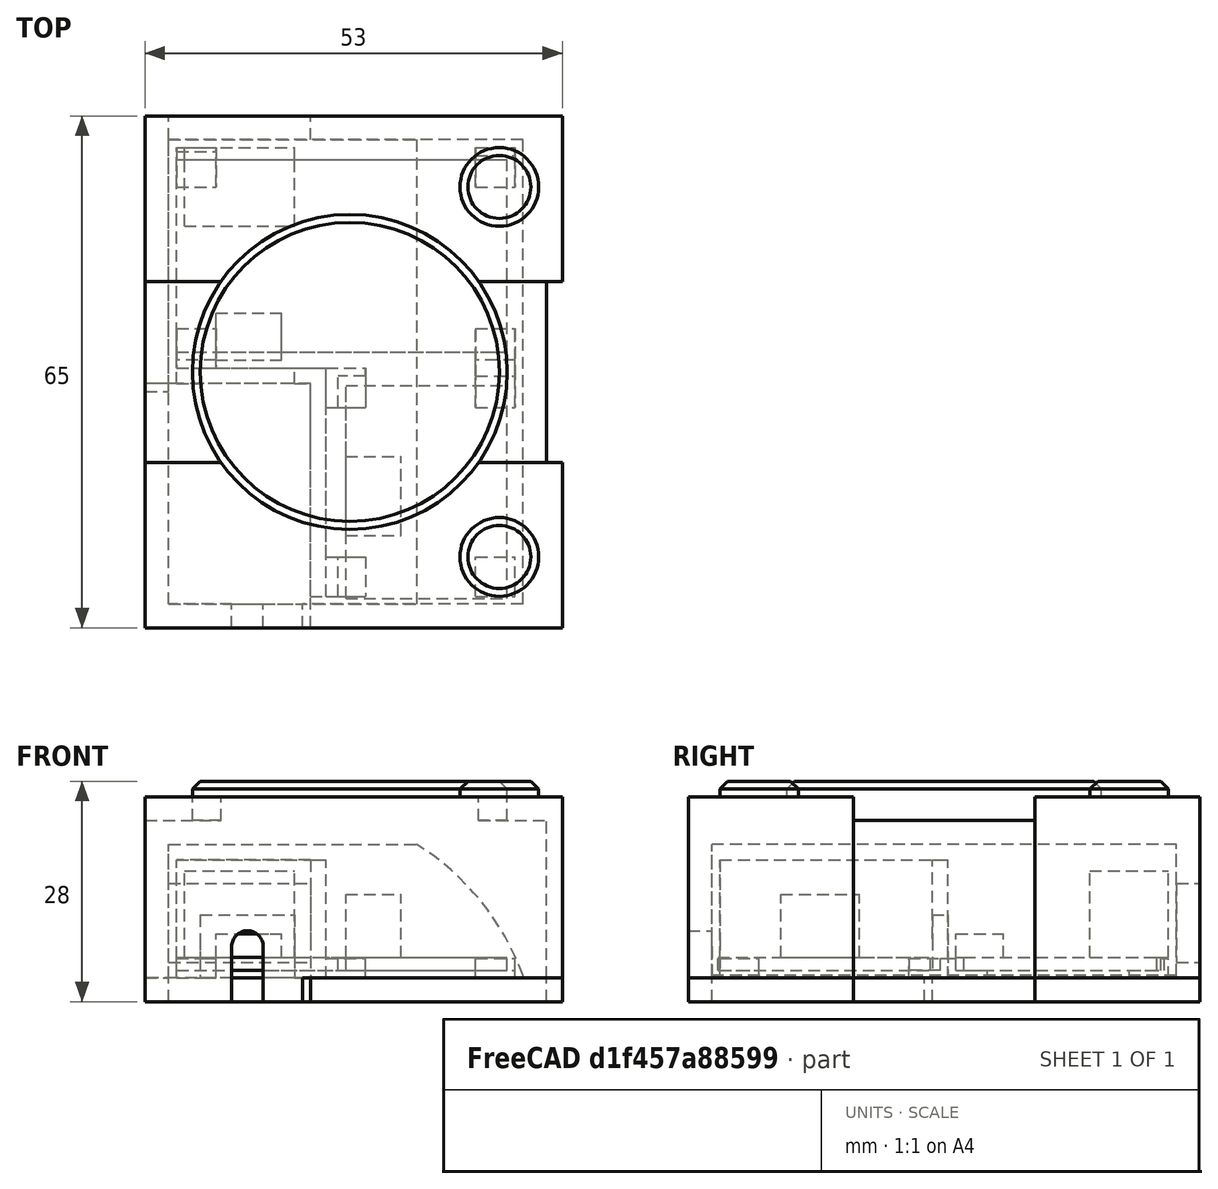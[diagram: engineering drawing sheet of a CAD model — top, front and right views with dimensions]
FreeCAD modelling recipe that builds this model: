
FCSTD DOCUMENT  (FreeCAD 0.17R13522 (Git))
Label: ps1
License: All rights reserved
LicenseURL: http://en.wikipedia.org/wiki/All_rights_reserved
objects: Part::Box×35, Part::Cut×16, Part::MultiFuse×8, PartDesign::FeatureBase×4, Part::Cylinder×4, Part::Fillet×2, App::DocumentObjectGroup×1, Part::MultiCommon×1, Part::Chamfer×1
note: 71 computed .brp shape members not serialized (recipe doc carries the construction recipe); baked Part::Feature solids carry a one-line shape summary decoded from their .brp

FEATURE [Part::Box] Box  label="Cube"
  AttacherType = Attacher::AttachEngine3D
  Height = 1.6
  Length = 42
  Width = 24.5
FEATURE [Part::Box] Box001  label="Cube001"
  AttacherType = Attacher::AttachEngine3D
  Height = 11
  Length = 14
  Placement = pos=(1,16,1.6) rot=(0,0,1;0rad)
  Width = 10
FEATURE [Part::Box] Box002  label="Cube002"
  AttacherType = Attacher::AttachEngine3D
  Height = 3
  Length = 8.3
  Placement = pos=(5,-1,1.6) rot=(0,0,1;0rad)
  Width = 6
FEATURE [Part::MultiFuse] Fusion  label="mcu_pcb"
  Placement = pos=(0,-51,0) rot=(0,0,1;0rad)
  Shapes = -> [Box,Box001,Box002]
FEATURE [Part::Box] Box003  label="Cube003"
  AttacherType = Attacher::AttachEngine3D
  Height = 1.6
  Length = 20.5
  Width = 27
FEATURE [Part::Box] Box004  label="Cube004"
  AttacherType = Attacher::AttachEngine3D
  Height = 8
  Length = 7
  Placement = pos=(0,8,1.6) rot=(0,0,1;0rad)
  Width = 10
FEATURE [Part::MultiFuse] Fusion001  label="imu_pcb001"
  Placement = pos=(21.5,-82.25,0) rot=(0,0,1;0rad)
  Shapes = -> [Box003,Box004]
FEATURE [App::DocumentObjectGroup] Group001  label="boards"
  Group = -> [Fusion,Fusion001]
FEATURE [Part::Box] Box005  label="Cube005"
  AttacherType = Attacher::AttachEngine3D
  Height = 23
  Length = 51
  Placement = pos=(-4,-65,-4) rot=(0,0,1;0rad)
  Width = 23
FEATURE [Part::Box] Box006  label="Cube006"
  AttacherType = Attacher::AttachEngine3D
  Height = 26
  Length = 53
  Placement = pos=(-4,-42,-4) rot=(0,0,1;0rad)
  Width = 21
FEATURE [PartDesign::FeatureBase] Clone
  BaseFeature = -> Box006
  Placement = pos=(-4,-86,-4) rot=(0,0,1;0rad)
FEATURE [Part::Cylinder] Cylinder
  Angle = 360
  AttacherType = Attacher::AttachEngine3D
  Height = 5
  Placement = pos=(22,-53.5,19) rot=(0,0,1;0rad)
  Radius = 20
FEATURE [Part::Cylinder] Cylinder001
  Angle = 360
  AttacherType = Attacher::AttachEngine3D
  Height = 5
  Placement = pos=(41,-30,19) rot=(0,0,1;0rad)
  Radius = 5
FEATURE [PartDesign::FeatureBase] Clone001
  BaseFeature = -> Cylinder001
  Placement = pos=(41,-77,19) rot=(0,0,1;0rad)
FEATURE [Part::MultiFuse] Fusion002
  Shapes = -> [Box005,Clone,Box006,Cylinder,Cylinder001,Clone001]
FEATURE [Part::Box] Box007  label="Cube007"
  AttacherType = Attacher::AttachEngine3D
  Height = 20
  Length = 45
  Placement = pos=(-1,-83,-4) rot=(0,0,1;0rad)
  Width = 59
FEATURE [Part::Fillet] Fillet
  Base = -> Fusion002
  Edges = 3 edges r=1: [Edge33,Edge35,Edge57]
FEATURE [Part::Fillet] Fillet001
  Base = -> Fillet
  Edges = 8 edges r=2: [Edge15,Edge22,Edge23,Edge24,Edge32,Edge33,Edge35,Edge38]
FEATURE [Part::Box] Box008  label="Cube008"
  AttacherType = Attacher::AttachEngine3D
  Height = 3
  Length = 62
  Placement = pos=(-8,-92,-4) rot=(0,0,1;0rad)
  Width = 77
FEATURE [PartDesign::FeatureBase] Clone002
  BaseFeature = -> Fillet001
FEATURE [PartDesign::FeatureBase] Clone003
  BaseFeature = -> Box008
  Placement = pos=(-8,-92,-4) rot=(0,0,1;0rad)
FEATURE [Part::MultiCommon] Common  label="bottom"
  Shapes = -> [Clone003,Clone002]
FEATURE [Part::MultiFuse] Fusion003
  Shapes = -> [Box005,Clone,Box006,Cylinder,Cylinder001,Clone001]
FEATURE [Part::Cut] Cut  label="top"
  Base = -> Fusion003
  Tool = -> Box008
FEATURE [Part::Cut] Cut001
  Base = -> Cut
  Tool = -> Box007
FEATURE [Part::Cylinder] Cylinder002
  Angle = 360
  AttacherType = Attacher::AttachEngine3D
  Height = 10
  Placement = pos=(9,-89,3) rot=(1,0,0;-1.5708rad)
  Radius = 2
FEATURE [Part::Box] Box009  label="Cube009"
  AttacherType = Attacher::AttachEngine3D
  Height = 5
  Length = 4
  Placement = pos=(7,-89,-2) rot=(0,0,1;0rad)
  Width = 10
FEATURE [Part::MultiFuse] Fusion004
  Shapes = -> [Cylinder002,Box009]
FEATURE [Part::Cut] Cut002
  Base = -> Cut001
  Tool = -> Fusion004
FEATURE [Part::Box] Box010  label="Cube010"
  AttacherType = Attacher::AttachEngine3D
  Height = 10
  Length = 18
  Placement = pos=(-1,-25,1) rot=(0,0,1;0rad)
  Width = 13
FEATURE [Part::Cut] Cut003
  Base = -> Cut002
  Tool = -> Box010
FEATURE [Part::Box] Box011  label="Cube011"
  AttacherType = Attacher::AttachEngine3D
  Height = 15
  Length = 19
  Placement = pos=(0,-82,-1) rot=(0,0,1;0rad)
  Width = 29
FEATURE [Part::Box] Box012  label="Cube012"
  AttacherType = Attacher::AttachEngine3D
  Height = 16
  Length = 19
  Placement = pos=(-2,-84,-1) rot=(0,0,1;0rad)
  Width = 29
FEATURE [Part::Cut] Cut004
  Base = -> Box011
  Tool = -> Box012
FEATURE [Part::Box] Box013  label="Cube013"
  AttacherType = Attacher::AttachEngine3D
  Height = 9
  Length = 12
  Placement = pos=(3,-59,-2) rot=(0,0,1;0rad)
  Width = 12
FEATURE [Part::Cut] Cut005
  Base = -> Cut004
  Tool = -> Box013
FEATURE [Part::Box] Box014  label="Cube014"
  AttacherType = Attacher::AttachEngine3D
  Height = 3.5
  Length = 5
  Placement = pos=(0,-30,-2) rot=(0,0,1;0rad)
  Width = 5
FEATURE [Part::Box] Box015  label="Cube015"
  AttacherType = Attacher::AttachEngine3D
  Height = 3.5
  Length = 5
  Placement = pos=(38,-30,-2) rot=(0,0,1;0rad)
  Width = 5
FEATURE [Part::Box] Box016  label="Cube016"
  AttacherType = Attacher::AttachEngine3D
  Height = 3.5
  Length = 5
  Placement = pos=(0,-53,-2) rot=(0,0,1;0rad)
  Width = 5
FEATURE [Part::Box] Box017  label="Cube017"
  AttacherType = Attacher::AttachEngine3D
  Height = 3.5
  Length = 5
  Placement = pos=(38,-53,-2) rot=(0,0,1;0rad)
  Width = 5
FEATURE [Part::Box] Box018  label="Cube018"
  AttacherType = Attacher::AttachEngine3D
  Height = 3.5
  Length = 5
  Placement = pos=(38,-58,-2) rot=(0,0,1;0rad)
  Width = 5
FEATURE [Part::Box] Box019  label="Cube019"
  AttacherType = Attacher::AttachEngine3D
  Height = 3.5
  Length = 5
  Placement = pos=(19,-58,-2) rot=(0,0,1;0rad)
  Width = 5
FEATURE [Part::Box] Box020  label="Cube020"
  AttacherType = Attacher::AttachEngine3D
  Height = 3.5
  Length = 5
  Placement = pos=(19,-82,-2) rot=(0,0,1;0rad)
  Width = 5
FEATURE [Part::Box] Box021  label="Cube021"
  AttacherType = Attacher::AttachEngine3D
  Height = 3.5
  Length = 5
  Placement = pos=(38,-82,-2) rot=(0,0,1;0rad)
  Width = 5
FEATURE [Part::Box] Box022  label="Cube022"
  AttacherType = Attacher::AttachEngine3D
  Height = 3.5
  Length = 5
  Placement = pos=(0,-30.5,0) rot=(0,0,1;0rad)
  Width = 5
FEATURE [Part::Cut] Cut006
  Base = -> Box014
  Tool = -> Box022
FEATURE [Part::Box] Box023  label="Cube023"
  AttacherType = Attacher::AttachEngine3D
  Height = 3.5
  Length = 5
  Placement = pos=(38,-31,0) rot=(0,0,1;0rad)
  Width = 5
FEATURE [Part::Cut] Cut007
  Base = -> Box015
  Tool = -> Box023
FEATURE [Part::Box] Box024  label="Cube024"
  AttacherType = Attacher::AttachEngine3D
  Height = 3.5
  Length = 5
  Placement = pos=(0,-52,0) rot=(0,0,1;0rad)
  Width = 5
FEATURE [Part::Cut] Cut008
  Base = -> Box016
  Tool = -> Box024
FEATURE [Part::Box] Box025  label="Cube025"
  AttacherType = Attacher::AttachEngine3D
  Height = 3.5
  Length = 5
  Placement = pos=(38,-52,0) rot=(0,0,1;0rad)
  Width = 5
FEATURE [Part::Cut] Cut009
  Base = -> Box017
  Tool = -> Box025
FEATURE [Part::Box] Box026  label="Cube026"
  AttacherType = Attacher::AttachEngine3D
  Height = 3.5
  Length = 5
  Placement = pos=(38,-59,0) rot=(0,0,1;0rad)
  Width = 5
FEATURE [Part::Cut] Cut010
  Base = -> Box018
  Tool = -> Box026
FEATURE [Part::Box] Box027  label="Cube027"
  AttacherType = Attacher::AttachEngine3D
  Height = 3.5
  Length = 5
  Placement = pos=(20.5,-59,0) rot=(0,0,1;0rad)
  Width = 5
FEATURE [Part::Cut] Cut011
  Base = -> Box019
  Tool = -> Box027
FEATURE [Part::Box] Box028  label="Cube028"
  AttacherType = Attacher::AttachEngine3D
  Height = 3.5
  Length = 5
  Placement = pos=(20.5,-82,0) rot=(0,0,1;0rad)
  Width = 5
FEATURE [Part::Cut] Cut012
  Base = -> Box020
  Tool = -> Box028
FEATURE [Part::Box] Box029  label="Cube029"
  AttacherType = Attacher::AttachEngine3D
  Height = 3.5
  Length = 5
  Placement = pos=(38,-82,0) rot=(0,0,1;0rad)
  Width = 5
FEATURE [Part::Cut] Cut013
  Base = -> Box021
  Tool = -> Box029
FEATURE [Part::MultiFuse] Fusion005
  Shapes = -> [Cut013,Cut012,Cut011,Cut010,Cut009,Cut008,Cut007,Cut006,Cut005,Common]
FEATURE [Part::Chamfer] Chamfer
  Base = -> Cut003
  Edges = 3 edges r=1: [Edge51,Edge53,Edge95]
  Placement = pos=(0,0,44) rot=(0,0,1;0rad)
FEATURE [Part::Box] Box030  label="Cube030"
  AttacherType = Attacher::AttachEngine3D
  Height = 10
  Length = 26
  Placement = pos=(-9,-90,-6) rot=(0,0,1;0rad)
  Width = 35
FEATURE [Part::Cut] Cut014
  Base = -> Fusion005
  Tool = -> Box030
FEATURE [Part::Box] Box031  label="Cube031"
  AttacherType = Attacher::AttachEngine3D
  Height = 18
  Length = 14
  Placement = pos=(30,-84,43) rot=(0,0,1;0rad)
  Width = 61
FEATURE [Part::Cylinder] Cylinder003
  Angle = 360
  AttacherType = Attacher::AttachEngine3D
  Height = 67
  Placement = pos=(13,-20,32) rot=(1,0,0;1.5708rad)
  Radius = 33
FEATURE [Part::Cut] Cut015
  Base = -> Box031
  Tool = -> Cylinder003
FEATURE [Part::MultiFuse] Fusion006
  Placement = pos=(0,0,-44) rot=(0,0,1;0rad)
  Shapes = -> [Chamfer,Cut015]
FEATURE [Part::Box] Box032  label="Cube032"
  AttacherType = Attacher::AttachEngine3D
  Height = 3
  Length = 3
  Placement = pos=(-4,-86,-4) rot=(0,0,1;0rad)
  Width = 30
FEATURE [Part::Box] Box033  label="Cube033"
  AttacherType = Attacher::AttachEngine3D
  Height = 3
  Length = 11
  Placement = pos=(-4,-86,-4) rot=(0,0,1;0rad)
  Width = 3
FEATURE [Part::Box] Box034  label="Cube034"
  AttacherType = Attacher::AttachEngine3D
  Height = 3
  Length = 5
  Placement = pos=(11,-86,-4) rot=(0,0,1;0rad)
  Width = 3
FEATURE [Part::MultiFuse] Fusion007
  Shapes = -> [Fusion006,Box032,Box033,Box034]
